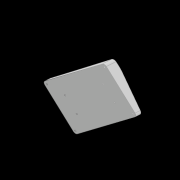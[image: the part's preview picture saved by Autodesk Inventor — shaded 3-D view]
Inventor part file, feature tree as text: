
AUTODESK INVENTOR PART (.ipt)
format: ipt  version: 2020 (Build 240168000, 168)  size: 279,040 bytes
history: native  units: in
note: dims shown in document units (in); Inventor stores cm internally (conversion verified against a paired STEP export)
features: other x4, extrude x1
ambient origin geometry x8: Origin, YZ Plane, XZ Plane, XY Plane, X Axis, Y Axis, Z Axis, Center Point
bodies: Solid1 (feature_tree)
feature tree (5):
  other  "switchback.ipt"
  extrude  "ArduinoMountFeature"  Depth=0.3937in
  other  "Solid67::switchback.ipt"
  other  "TaggingFeature1"
  other  "ArduinoMount"
